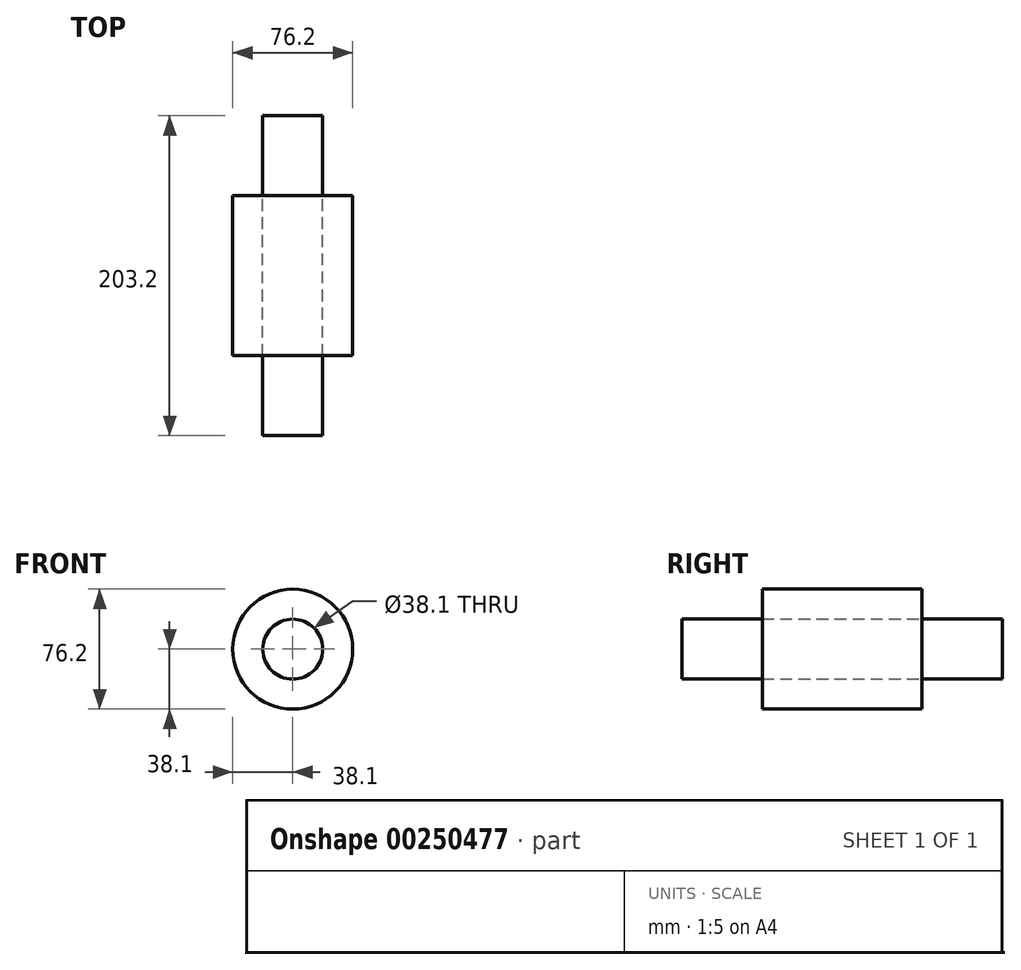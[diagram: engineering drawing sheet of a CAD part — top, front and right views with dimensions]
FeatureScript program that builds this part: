
annotation { "Feature Type Name" : "Feature", "Feature Type Description" : "" }
export const myFeature = defineFeature(function(context is Context, id is Id, definition is map)
    precondition{}
    {
        {
            var Q0;
            Q0=qCreatedBy(makeId("Front.planeOp"),FACE);
            var sketch = newSketch(context, id + "F0", { "sketchPlane" : qUnion([Q0])});
            skCircle(sketch, "E0", {"center": v(0, 0) * mm, "radius": 38.1 * mm});
            skCircle(sketch, "E1", {"center": v(0, 0) * mm, "radius": 19.05 * mm});
            skSolve(sketch);
        }
        {
            var Q0;
            Q0 = qSketchRegion(id + "F2", true);
            var Q1;
            Q1=makeQuery(id+"F0.imprint","IMPRINT",FACE,{"disambiguationData":[TD([[makeQuery(id+"F0.imprint","IMPRINT",EDGE,{"derivedFrom":sQuery(id+"F0.wireOp",EDGE,"E0")}),1.0]])]});
            extrude(context, id + "F1", {"entities" : qUnion([Q0, Q1]), "endBound" : BoundingType.SYMMETRIC, "depth" : 101.6 * mm});
        }
        {
            var Q0;
            Q0=makeQuery(id+"F0.imprint","IMPRINT",FACE,{"disambiguationData":[TD([[makeQuery(id+"F0.imprint","IMPRINT",EDGE,{"derivedFrom":sQuery(id+"F0.wireOp",EDGE,"E1")}),1.0]])]});
            var sketch = newSketch(context, id + "F2", { "sketchPlane" : qUnion([Q0])});
            skSolve(sketch);
        }
        {
            var Q0;
            Q0 = qSketchRegion(id + "F2", true);
            var Q1;
            Q1=makeQuery(id+"F2.imprint","IMPRINT",FACE,{"disambiguationData":[TD([[makeQuery(id+"F2.imprint","IMPRINT",EDGE,{"derivedFrom":makeQuery(id+"F0.imprint","IMPRINT",EDGE,{"derivedFrom":sQuery(id+"F0.wireOp",EDGE,"E1")})}),1.0]])]});
            extrude(context, id + "F3", {"entities" : qUnion([Q0, Q1]), "endBound" : BoundingType.SYMMETRIC, "depth" : 203.2 * mm});
        }
    });
